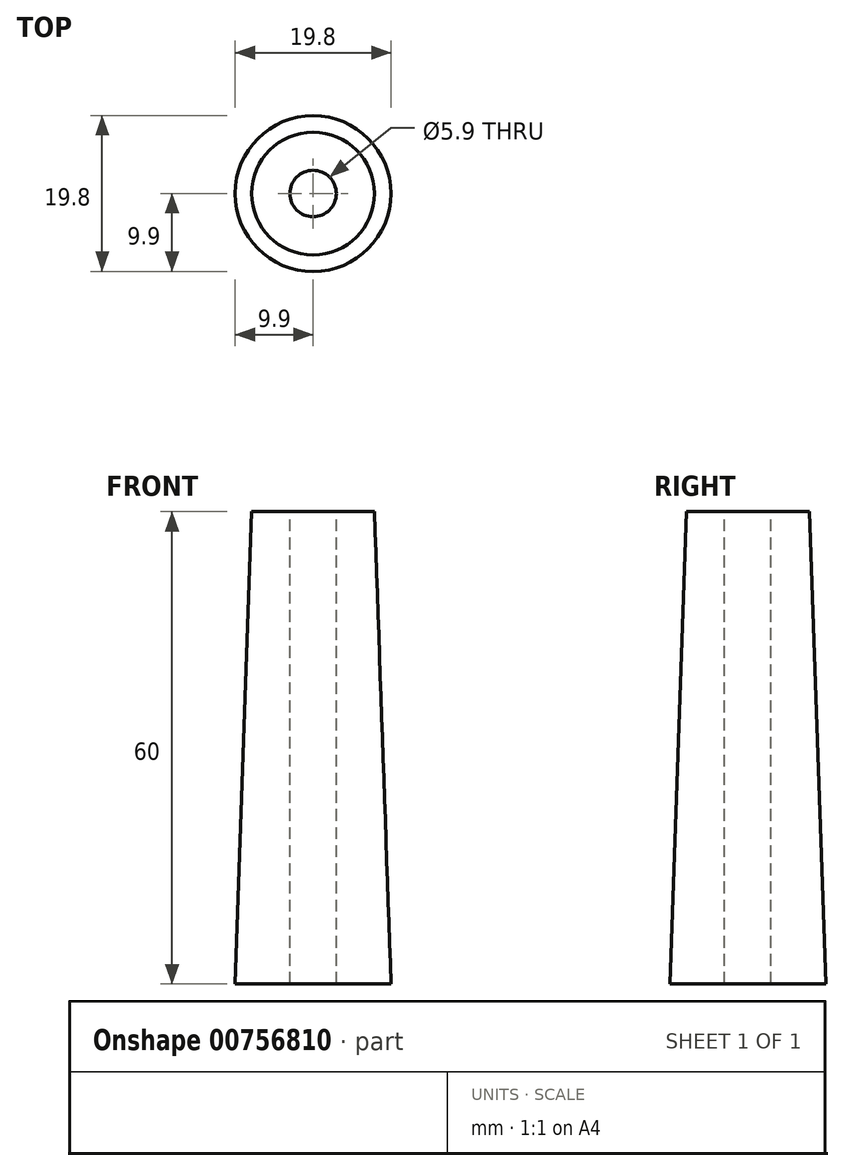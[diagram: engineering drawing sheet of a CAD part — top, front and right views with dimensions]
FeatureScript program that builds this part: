
annotation { "Feature Type Name" : "Feature", "Feature Type Description" : "" }
export const myFeature = defineFeature(function(context is Context, id is Id, definition is map)
    precondition{}
    {
        {
            var Q0;
            Q0=qCreatedBy(makeId("Top.planeOp"),FACE);
            var sketch = newSketch(context, id + "F0", { "sketchPlane" : qUnion([Q0])});
            skCircle(sketch, "E0", {"center": v(0, 0) * mm, "radius": 9.9 * mm});
            skSolve(sketch);
        }
        {
            var Q0;
            Q0=qCreatedBy(makeId("Top.planeOp"),FACE);
            cPlane(context, id + "F1", {"entities" : qUnion([Q0]), "cplaneType" : CPlaneType.OFFSET, "offset" : 60 * mm, "width" : 152.4 * mm, "height" : 152.4 * mm});
        }
        {
            var Q0;
            Q0=qCreatedBy(id+"F1.planeOp",FACE);
            var sketch = newSketch(context, id + "F2", { "sketchPlane" : qUnion([Q0])});
            skCircle(sketch, "E1", {"center": v(0, 0) * mm, "radius": 7.8 * mm});
            skSolve(sketch);
        }
        {
            var Q0;
            Q0=makeQuery(id+"F0.imprint","IMPRINT",FACE,{"disambiguationData":[TD([[makeQuery(id+"F0.imprint","IMPRINT",EDGE,{"derivedFrom":sQuery(id+"F0.wireOp",EDGE,"E0")}),1.0]])]});
            var Q1;
            Q1=makeQuery(id+"F2.imprint","IMPRINT",FACE,{"disambiguationData":[TD([[makeQuery(id+"F2.imprint","IMPRINT",EDGE,{"derivedFrom":sQuery(id+"F2.wireOp",EDGE,"E1")}),1.0]])]});
            loft(context, id + "F3", {"sheetProfilesArray" : [{ "sheetProfileEntities" : qUnion([Q0]) }, { "sheetProfileEntities" : qUnion([Q1]) }]});
        }
        {
            var Q0;
            Q0=makeQuery(id+"F3.opLoft","CAP_FACE",FACE,{"disambiguationData":[OSD([makeQuery(id+"F2.imprint","IMPRINT",FACE,{"disambiguationData":[TD([[makeQuery(id+"F2.imprint","IMPRINT",EDGE,{"derivedFrom":sQuery(id+"F2.wireOp",EDGE,"E1")}),1.0]])]})])],"isStart":true});
            var sketch = newSketch(context, id + "F4", { "sketchPlane" : qUnion([Q0])});
            skCircle(sketch, "E2", {"center": v(0, 0) * mm, "radius": 2.95 * mm});
            skSolve(sketch);
        }
        {
            var Q0;
            Q0=makeQuery(id+"F4.imprint","IMPRINT",FACE,{"disambiguationData":[TD([[makeQuery(id+"F4.imprint","IMPRINT",EDGE,{"derivedFrom":sQuery(id+"F4.wireOp",EDGE,"E2")}),1.0]])]});
            extrude(context, id + "F5", {"entities" : qUnion([Q0]), "operationType" : NewBodyOperationType.REMOVE, "endBound" : BoundingType.THROUGH_ALL, "oppositeDirection" : true, "depth" : 25.4 * mm, "offsetDistance" : 25.4 * mm});
        }
    });
